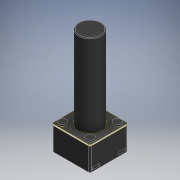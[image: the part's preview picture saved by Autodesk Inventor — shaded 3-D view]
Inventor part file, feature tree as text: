
AUTODESK INVENTOR PART (.ipt)
format: ipt  version: 2021 (Build 250183000, 183)  size: 212,992 bytes
history: native  units: mm
features: sketch x6, extrude x4, plane x2, fillet x2, other x1, revolve x1, pattern_linear x1
ambient origin geometry x8: Origin, YZ Plane, XZ Plane, XY Plane, X Axis, Y Axis, Z Axis, Center Point
bodies: Solid1 (feature_tree), Solid2 (feature_tree)
feature tree (17):
  extrude  "Extrusion1"  Depth=5.0mm
  sketch  "Sketch2"  dims[d5=3.0mm d6=11.0mm d7=0.0mm]
  extrude  "Extrusion2"  Depth=3.2mm
  extrude  "Extrusion3"  Depth=11.0mm TaperAngle=0.0deg
  sketch  "Sketch3"  dims[d8=0.2mm d9=0.0mm d10=1.0mm]
  other  "Work Point1"
  sketch  "Sketch4"  dims[d11=1.8mm d12=0.2mm]
  plane  "Work Plane2"
  revolve  "Revolution1"  [1 undecoded]
  sketch  "Sketch Driven Pattern1"  dims[d0=5.0mm d1=5.0mm]
  extrude  "Extrusion4"  Depth=0.2mm
  pattern_linear  "Rectangular Pattern1"  Spacing1=0.1mm  [1 undecoded]
  fillet  "Fillet1"  Radius=0.2mm
  fillet  "Fillet2"  [1 undecoded]
  sketch  "Sketch1"  dims[d2=3.0mm d3=0.0mm d4=3.2mm]
  plane  "Work Plane1"
  sketch  "Sketch6"  dims[d13=0.15mm d14=0.1mm d17=0.2mm d18=90.0deg d19=1.0mm d20=0.3mm d21=0.3mm d22=0.2mm d23=1.0mm d24=0.0mm d25=20.0mm d27=3.4mm d28=20.0mm d30=4.0mm d31=0.2mm d32=0.1mm]
note: 3 required parameter values undecoded (feature->parameter linkage not recoverable at this tier; creation-order binding heuristic only, values carry confidence <= 0.55)